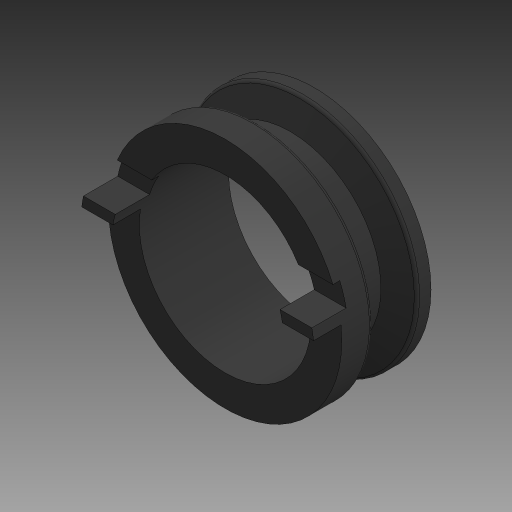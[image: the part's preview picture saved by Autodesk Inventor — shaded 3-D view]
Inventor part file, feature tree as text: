
AUTODESK INVENTOR PART (.ipt)
format: ipt  version: 2023 (Build 270158000, 158)  size: 427,520 bytes
history: native  units: mm
features: sketch x5, other x3, extrude x3, projected_geometry x2, fillet x1
ambient origin geometry x8: Origin, YZ Plane, XZ Plane, XY Plane, X Axis, Y Axis, Z Axis, Center Point
bodies: Body1 (feature_tree)
feature tree (14):
  other  "Těleso1"
  extrude  "Vysunutí1"  Depth=34.0mm
  other  "Rotace1"
  extrude  "Vysunutí2"  Depth=13.0mm TaperAngle=0.0deg
  other  "Rotace2"
  fillet  "Zaoblení1"  Radius=25.0mm
  extrude  "Vysunutí4"  TaperAngle=360.0deg  [1 undecoded]
  sketch  "Náčrt1"
  sketch  "Náčrt2"
  projected_geometry  "Promítnutá smyčka1"
  projected_geometry  "Promítnutá smyčka2"
  sketch  "Náčrt4"
  sketch  "Náčrt5"
  sketch  "Náčrt6"
note: 1 required parameter value undecoded (feature->parameter linkage not recoverable at this tier; creation-order binding heuristic only, values carry confidence <= 0.55)
